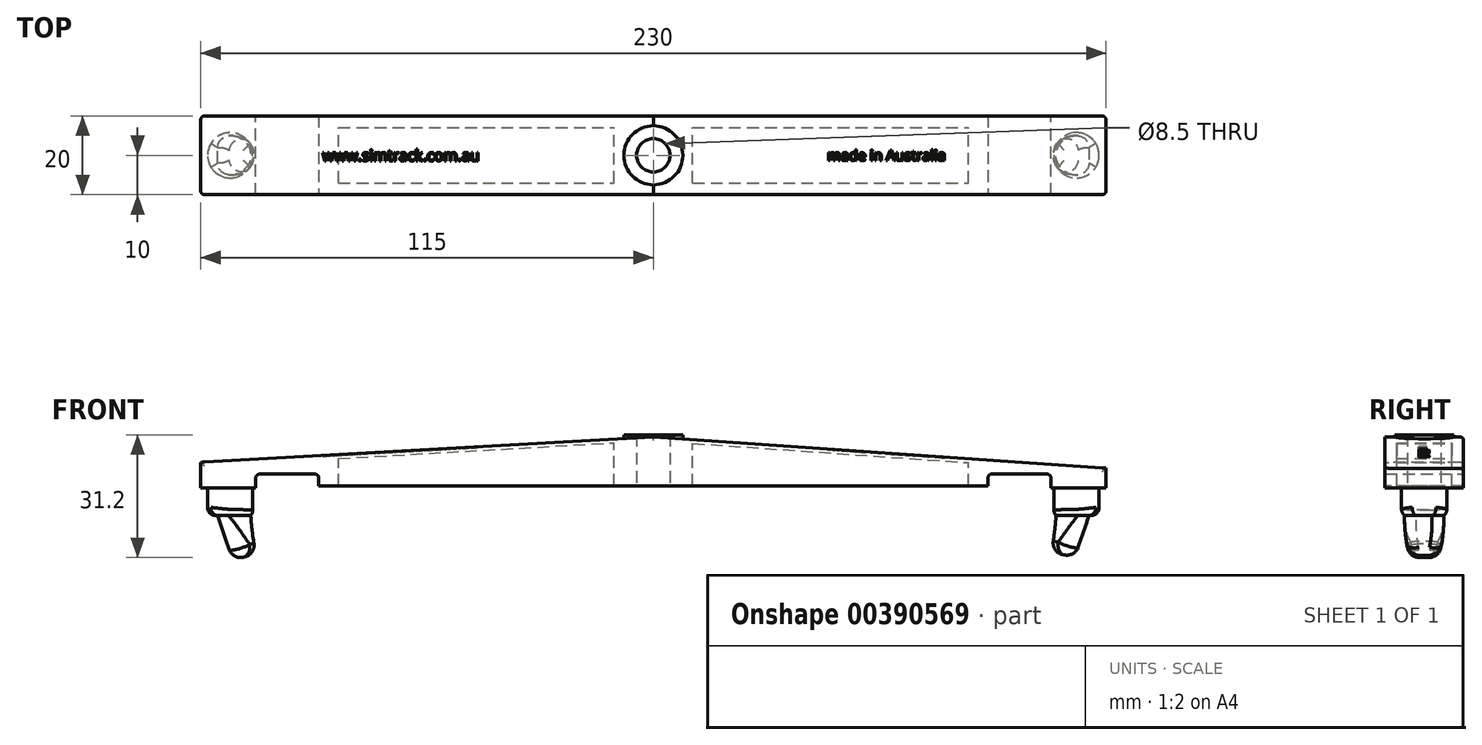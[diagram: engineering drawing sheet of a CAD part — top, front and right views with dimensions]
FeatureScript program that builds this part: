
annotation { "Feature Type Name" : "Feature", "Feature Type Description" : "" }
export const myFeature = defineFeature(function(context is Context, id is Id, definition is map)
    precondition{}
    {
        {
            var Q0;
            Q0=qCreatedBy(makeId("Top.planeOp"),FACE);
            var sketch = newSketch(context, id + "F0", { "sketchPlane" : qUnion([Q0])});
            skCircle(sketch, "E0", {"center": v(0, 0) * mm, "radius": 4.25 * mm});
            skLineSegment(sketch, "E1.bottom", {"start": v(115, -10) * mm, "end": v(-115, -10) * mm});
            skLineSegment(sketch, "E1.top", {"start": v(115, 10) * mm, "end": v(-115, 10) * mm});
            skLineSegment(sketch, "E1.left", {"start": v(115, -10) * mm, "end": v(115, 10) * mm});
            skLineSegment(sketch, "E1.right", {"start": v(-115, -10) * mm, "end": v(-115, 10) * mm});
            skPoint(sketch, "E2.visualSharp", {"position": v(-115, 10) * mm});
            skLineSegment(sketch, "E2.filletArc", {"start": v(-115, 10) * mm, "end": v(-115, 10) * mm});
            skPoint(sketch, "E3.visualSharp", {"position": v(-115, -10) * mm});
            skLineSegment(sketch, "E3.filletArc", {"start": v(-115, -10) * mm, "end": v(-115, -10) * mm});
            skPoint(sketch, "E4.visualSharp", {"position": v(115, 10) * mm});
            skLineSegment(sketch, "E4.filletArc", {"start": v(115, 10) * mm, "end": v(115, 10) * mm});
            skPoint(sketch, "E5.visualSharp", {"position": v(115, -10) * mm});
            skLineSegment(sketch, "E5.filletArc", {"start": v(115, -10) * mm, "end": v(115, -10) * mm});
            skLineSegment(sketch, "E6.bottom", {"start": v(80, 7) * mm, "end": v(10, 7) * mm});
            skLineSegment(sketch, "E6.top", {"start": v(80, -7) * mm, "end": v(10, -7) * mm});
            skLineSegment(sketch, "E6.left", {"start": v(80, 7) * mm, "end": v(80, -7) * mm});
            skLineSegment(sketch, "E6.right", {"start": v(10, 7) * mm, "end": v(10, -7) * mm});
            skLineSegment(sketch, "E7.bottom", {"start": v(-10, 7) * mm, "end": v(-80, 7) * mm});
            skLineSegment(sketch, "E7.top", {"start": v(-10, -7) * mm, "end": v(-80, -7) * mm});
            skLineSegment(sketch, "E7.left", {"start": v(-10, 7) * mm, "end": v(-10, -7) * mm});
            skLineSegment(sketch, "E7.right", {"start": v(-80, 7) * mm, "end": v(-80, -7) * mm});
            skCircle(sketch, "E8", {"center": v(0, 0) * mm, "radius": 7.5 * mm});
            skSolve(sketch);
        }
        {
            var Q0;
            Q0=makeQuery(id+"F0.imprint","IMPRINT",FACE,{"disambiguationData":[TD([[makeQuery(id+"F0.imprint","IMPRINT",EDGE,{"derivedFrom":sQuery(id+"F0.wireOp",EDGE,"E1.bottom")}),-1.0]])]});
            var Q1;
            Q1=makeQuery(id+"F0.imprint","IMPRINT",FACE,{"disambiguationData":[TD([[makeQuery(id+"F0.imprint","IMPRINT",EDGE,{"derivedFrom":sQuery(id+"F0.wireOp",EDGE,"q9BRd2um-oMs7-7MK2-WjCr-aT8UQEt5jsp8")}),-1.0]])]});
            var Q2;
            {var subQ0=sQuery(id+"F0.wireOp",EDGE,"CfEYtvD2-7vdv-HU4w-jJwD-IvnwvT9jjSvh.right");var subQ1=sQuery(id+"F0.wireOp",EDGE,"TnjMtal5-3gMc-DNrO-T4Mg-M14iXYZFMKTD");var subQ2=makeQuery(id+"F0.imprint","INTERSECT",VERTEX,{"disambiguationData":[OD(0.0)],"derivedFrom":[subQ1,subQ0]});Q2=makeQuery(id+"F0.imprint","IMPRINT",FACE,{"disambiguationData":[TD([[makeQuery(id+"F0.imprint","IMPRINT",EDGE,{"disambiguationData":[TD([[subQ2,1.0]])],"derivedFrom":subQ1}),1.0]])]});}
            var Q3;
            {var subQ0=sQuery(id+"F0.wireOp",EDGE,"CfEYtvD2-7vdv-HU4w-jJwD-IvnwvT9jjSvh.left");var subQ1=sQuery(id+"F0.wireOp",EDGE,"O0jPoW7s-RU5z-iA6U-w5ju-wIfl1B3ZVbkh");var subQ2=makeQuery(id+"F0.imprint","INTERSECT",VERTEX,{"disambiguationData":[OD(0.0)],"derivedFrom":[subQ1,subQ0]});Q3=makeQuery(id+"F0.imprint","IMPRINT",FACE,{"disambiguationData":[TD([[makeQuery(id+"F0.imprint","IMPRINT",EDGE,{"disambiguationData":[TD([[subQ2,-1.0]])],"derivedFrom":subQ1}),1.0]])]});}
            var Q4;
            {var subQ0=sQuery(id+"F0.wireOp",EDGE,"CfEYtvD2-7vdv-HU4w-jJwD-IvnwvT9jjSvh.right");var subQ1=sQuery(id+"F0.wireOp",EDGE,"TnjMtal5-3gMc-DNrO-T4Mg-M14iXYZFMKTD");var subQ2=makeQuery(id+"F0.imprint","INTERSECT",VERTEX,{"disambiguationData":[OD(0.0)],"derivedFrom":[subQ1,subQ0]});Q4=makeQuery(id+"F0.imprint","IMPRINT",FACE,{"disambiguationData":[TD([[makeQuery(id+"F0.imprint","IMPRINT",EDGE,{"disambiguationData":[TD([[subQ2,-1.0]])],"derivedFrom":subQ1}),1.0]])]});}
            var Q5;
            {var subQ0=sQuery(id+"F0.wireOp",EDGE,"CfEYtvD2-7vdv-HU4w-jJwD-IvnwvT9jjSvh.left");var subQ1=sQuery(id+"F0.wireOp",EDGE,"O0jPoW7s-RU5z-iA6U-w5ju-wIfl1B3ZVbkh");var subQ2=makeQuery(id+"F0.imprint","INTERSECT",VERTEX,{"disambiguationData":[OD(0.0)],"derivedFrom":[subQ1,subQ0]});Q5=makeQuery(id+"F0.imprint","IMPRINT",FACE,{"disambiguationData":[TD([[makeQuery(id+"F0.imprint","IMPRINT",EDGE,{"disambiguationData":[TD([[subQ2,1.0]])],"derivedFrom":subQ1}),1.0]])]});}
            extrude(context, id + "F1", {"entities" : qUnion([Q0, Q1, Q2, Q3, Q4, Q5]), "oppositeDirection" : true, "depth" : 5 * mm, "hasSecondDirection" : true, "secondDirectionOppositeDirection" : false, "secondDirectionDepth" : 8 * mm});
        }
        {
            var Q0;
            Q0=makeQuery(id+"F1.opExtrude","SWEPT_FACE",FACE,{"disambiguationData":[OSD([sQuery(id+"F0.wireOp",EDGE,"E1.bottom")])]});
            var sketch = newSketch(context, id + "F2", { "sketchPlane" : qUnion([Q0])});
            skLineSegment(sketch, "E9", {"start": v(-115, 1.5) * mm, "end": v(0, 8) * mm});
            skLineSegment(sketch, "E10", {"start": v(0, 8) * mm, "end": v(115, 0) * mm});
            skSolve(sketch);
        }
        {
            var Q0;
            {var subQ0=sQuery(id+"F2.wireOp",EDGE,"E10");Q0=makeQuery(id+"F2.imprint","IMPRINT",FACE,{"disambiguationData":[TD([[makeQuery(id+"F2.imprint","IMPRINT",EDGE,{"derivedFrom":subQ0}),1.0]])]});}
            var Q1;
            {var subQ0=sQuery(id+"F2.wireOp",EDGE,"E9");Q1=makeQuery(id+"F2.imprint","IMPRINT",FACE,{"disambiguationData":[TD([[makeQuery(id+"F2.imprint","IMPRINT",EDGE,{"derivedFrom":subQ0}),1.0]])]});}
            extrude(context, id + "F3", {"entities" : qUnion([Q0, Q1]), "operationType" : NewBodyOperationType.REMOVE, "oppositeDirection" : true, "depth" : 25 * mm});
        }
        {
            var Q0;
            Q0=makeQuery(id+"F0.imprint","IMPRINT",FACE,{"disambiguationData":[TD([[makeQuery(id+"F0.imprint","IMPRINT",EDGE,{"derivedFrom":sQuery(id+"F0.wireOp",EDGE,"E0")}),-1.0]])]});
            var Q1;
            Q1=makeQuery(id+"F0.imprint","IMPRINT",FACE,{"disambiguationData":[TD([[makeQuery(id+"F0.imprint","IMPRINT",EDGE,{"derivedFrom":sQuery(id+"F0.wireOp",EDGE,"E0")}),1.0]])]});
            extrude(context, id + "F4", {"entities" : qUnion([Q0, Q1]), "operationType" : NewBodyOperationType.ADD, "oppositeDirection" : true, "depth" : 5 * mm});
        }
        {
            var Q0;
            Q0=makeQuery(id+"F0.imprint","IMPRINT",FACE,{"disambiguationData":[TD([[makeQuery(id+"F0.imprint","IMPRINT",EDGE,{"derivedFrom":sQuery(id+"F0.wireOp",EDGE,"E0")}),1.0]])]});
            extrude(context, id + "F5", {"entities" : qUnion([Q0]), "operationType" : NewBodyOperationType.REMOVE, "depth" : 8 * mm, "hasSecondDirection" : true, "secondDirectionOppositeDirection" : true, "secondDirectionDepth" : 5 * mm});
        }
        {
            var Q0;
            Q0=makeQuery(id+"F1.opExtrude","SWEPT_FACE",FACE,{"disambiguationData":[OSD([sQuery(id+"F0.wireOp",EDGE,"E1.bottom")])]});
            var sketch = newSketch(context, id + "F6", { "sketchPlane" : qUnion([Q0])});
            skSolve(sketch);
        }
        {
            var Q0;
            Q0=makeQuery(id+"F1.opExtrude","SWEPT_FACE",FACE,{"disambiguationData":[OSD([sQuery(id+"F0.wireOp",EDGE,"E1.top")])]});
            var sketch = newSketch(context, id + "F7", { "sketchPlane" : qUnion([Q0])});
            skLineSegment(sketch, "E11", {"start": v(-115, -5) * mm, "end": v(-101, -5) * mm});
            skLineSegment(sketch, "E12", {"start": v(-101, -5) * mm, "end": v(-101, -1.5) * mm});
            skLineSegment(sketch, "E13", {"start": v(-101, -1.5) * mm, "end": v(-85, -1.5) * mm});
            skLineSegment(sketch, "E14", {"start": v(-85, -1.5) * mm, "end": v(-85, -5) * mm});
            skLineSegment(sketch, "E15", {"start": v(-85, -5) * mm, "end": v(-101, -5) * mm});
            skLineSegment(sketch, "E16", {"start": v(115, -5) * mm, "end": v(101, -5) * mm});
            skLineSegment(sketch, "E17", {"start": v(101, -5) * mm, "end": v(101, -1.5) * mm});
            skLineSegment(sketch, "E18", {"start": v(101, -1.5) * mm, "end": v(85, -1.5) * mm});
            skLineSegment(sketch, "E19", {"start": v(85, -1.5) * mm, "end": v(85, -5) * mm});
            skLineSegment(sketch, "E20", {"start": v(85, -5) * mm, "end": v(101, -5) * mm});
            skSolve(sketch);
        }
        {
            var Q0;
            Q0=makeQuery(id+"F7.imprint","IMPRINT",FACE,{"disambiguationData":[TD([[makeQuery(id+"F7.imprint","IMPRINT",EDGE,{"derivedFrom":sQuery(id+"F7.wireOp",EDGE,"E12")}),-1.0]])]});
            var Q1;
            Q1=makeQuery(id+"F7.imprint","IMPRINT",FACE,{"disambiguationData":[TD([[makeQuery(id+"F7.imprint","IMPRINT",EDGE,{"derivedFrom":sQuery(id+"F7.wireOp",EDGE,"E17")}),1.0]])]});
            extrude(context, id + "F8", {"entities" : qUnion([Q0, Q1]), "operationType" : NewBodyOperationType.REMOVE, "oppositeDirection" : true, "depth" : 25 * mm});
        }
        {
            var Q0;
            Q0=makeQuery(id+"F3.boolean.opBoolean","COPY",FACE,{"derivedFrom":makeQuery(id+"F3.opExtrude","SWEPT_FACE",FACE,{"disambiguationData":[OSD([sQuery(id+"F2.wireOp",EDGE,"E9")])]})});
            var sketch = newSketch(context, id + "F9", { "sketchPlane" : qUnion([Q0])});
            skCircle(sketch, "E21", {"center": v(-107.72, 0) * mm, "radius": 5 * mm});
            skSolve(sketch);
        }
        {
            var Q0;
            Q0=makeQuery(id+"F9.imprint","IMPRINT",FACE,{"disambiguationData":[TD([[makeQuery(id+"F9.imprint","IMPRINT",EDGE,{"derivedFrom":sQuery(id+"F9.wireOp",EDGE,"E21")}),1.0]])]});
            extrude(context, id + "F10", {"entities" : qUnion([Q0]), "operationType" : NewBodyOperationType.ADD, "oppositeDirection" : true, "depth" : 8 * mm});
        }
        {
            var Q0;
            Q0=makeQuery(id+"F3.boolean.opBoolean","COPY",FACE,{"derivedFrom":makeQuery(id+"F3.opExtrude","SWEPT_FACE",FACE,{"disambiguationData":[OSD([sQuery(id+"F2.wireOp",EDGE,"E10")])]})});
            var sketch = newSketch(context, id + "F11", { "sketchPlane" : qUnion([Q0])});
            skCircle(sketch, "E22", {"center": v(107.7, 0) * mm, "radius": 5 * mm});
            skSolve(sketch);
        }
        {
            var Q0;
            Q0=makeQuery(id+"F11.imprint","IMPRINT",FACE,{"disambiguationData":[TD([[makeQuery(id+"F11.imprint","IMPRINT",EDGE,{"derivedFrom":sQuery(id+"F11.wireOp",EDGE,"E22")}),1.0]])]});
            extrude(context, id + "F12", {"entities" : qUnion([Q0]), "operationType" : NewBodyOperationType.ADD, "oppositeDirection" : true, "depth" : 6 * mm});
        }
        {
            var Q0;
            Q0=makeQuery(id+"F0.imprint","IMPRINT",FACE,{"disambiguationData":[TD([[makeQuery(id+"F0.imprint","IMPRINT",EDGE,{"derivedFrom":sQuery(id+"F0.wireOp",EDGE,"E7.bottom")}),1.0]])]});
            var Q1;
            Q1=makeQuery(id+"F0.imprint","IMPRINT",FACE,{"disambiguationData":[TD([[makeQuery(id+"F0.imprint","IMPRINT",EDGE,{"derivedFrom":sQuery(id+"F0.wireOp",EDGE,"E6.bottom")}),1.0]])]});
            extrude(context, id + "F13", {"entities" : qUnion([Q0, Q1]), "operationType" : NewBodyOperationType.REMOVE, "depth" : 29 * mm, "hasDraft" : true, "draftAngle" : 3 * degree});
        }
        {
            var Q0;
            {var subQ0=sQuery(id+"F0.wireOp",EDGE,"E1.bottom");Q0=makeQuery(id+"F6.imprint","IMPRINT",FACE,{"disambiguationData":[TD([[makeQuery(id+"F6.imprint","IMPRINT",EDGE,{"derivedFrom":makeQuery(id+"F1.opExtrude","CAP_EDGE",EDGE,{"disambiguationData":[OSD([subQ0])],"isStart":false})}),-1.0]])]});}
            var sketch = newSketch(context, id + "F14", { "sketchPlane" : qUnion([Q0])});
            skSolve(sketch);
        }
        {
            var Q0;
            Q0=makeQuery(id+"F1.opExtrude","SWEPT_FACE",FACE,{"disambiguationData":[OSD([sQuery(id+"F0.wireOp",EDGE,"E1.top")])]});
            extrude(context, id + "F15", {"entities" : qUnion([Q0]), "operationType" : NewBodyOperationType.ADD, "oppositeDirection" : true, "depth" : 20 * mm});
        }
        {
            var Q0;
            Q0=makeQuery(id+"F0.imprint","IMPRINT",FACE,{"disambiguationData":[TD([[makeQuery(id+"F0.imprint","IMPRINT",EDGE,{"derivedFrom":sQuery(id+"F0.wireOp",EDGE,"E7.bottom")}),1.0]])]});
            var Q1;
            Q1=makeQuery(id+"F0.imprint","IMPRINT",FACE,{"disambiguationData":[TD([[makeQuery(id+"F0.imprint","IMPRINT",EDGE,{"derivedFrom":sQuery(id+"F0.wireOp",EDGE,"E6.bottom")}),1.0]])]});
            extrude(context, id + "F16", {"entities" : qUnion([Q0, Q1]), "operationType" : NewBodyOperationType.REMOVE, "oppositeDirection" : true, "depth" : 25 * mm, "hasSecondDirection" : true, "secondDirectionOppositeDirection" : false, "secondDirectionDepth" : 25 * mm});
        }
        {
            var Q0;
            Q0=makeQuery(id+"F0.imprint","IMPRINT",FACE,{"disambiguationData":[TD([[makeQuery(id+"F0.imprint","IMPRINT",EDGE,{"derivedFrom":sQuery(id+"F0.wireOp",EDGE,"E0")}),-1.0]])]});
            extrude(context, id + "F17", {"entities" : qUnion([Q0]), "operationType" : NewBodyOperationType.ADD, "depth" : 8.5 * mm});
        }
        {
            var Q0;
            Q0=makeQuery(id+"F0.imprint","IMPRINT",FACE,{"disambiguationData":[TD([[makeQuery(id+"F0.imprint","IMPRINT",EDGE,{"derivedFrom":sQuery(id+"F0.wireOp",EDGE,"E0")}),1.0]])]});
            extrude(context, id + "F18", {"entities" : qUnion([Q0]), "operationType" : NewBodyOperationType.REMOVE, "oppositeDirection" : true, "depth" : 25 * mm, "hasSecondDirection" : true, "secondDirectionOppositeDirection" : false, "secondDirectionDepth" : 25 * mm});
        }
        {
            var Q0;
            Q0=makeQuery(id+"F3.boolean.opBoolean","COPY",EDGE,{"derivedFrom":makeQuery(id+"F3.opExtrude","SWEPT_EDGE",EDGE,{"disambiguationData":[OSD([sQuery(id+"F0.wireOp",EDGE,"E1.bottom"),sQuery(id+"F0.wireOp",EDGE,"E1.left"),sQuery(id+"F2.wireOp",EDGE,"E10")])]})});
            var Q1;
            Q1=makeQuery(id+"F3.boolean.opBoolean","INTERSECT",EDGE,{"derivedFrom":[makeQuery(id+"F1.opExtrude","SWEPT_FACE",FACE,{"disambiguationData":[OSD([sQuery(id+"F0.wireOp",EDGE,"E1.top")])]}),makeQuery(id+"F3.opExtrude","SWEPT_FACE",FACE,{"disambiguationData":[OSD([sQuery(id+"F2.wireOp",EDGE,"E10")])]})]});
            var Q2;
            Q2=makeQuery(id+"F3.boolean.opBoolean","INTERSECT",EDGE,{"derivedFrom":[makeQuery(id+"F1.opExtrude","SWEPT_FACE",FACE,{"disambiguationData":[OSD([sQuery(id+"F0.wireOp",EDGE,"E1.top")])]}),makeQuery(id+"F3.opExtrude","SWEPT_FACE",FACE,{"disambiguationData":[OSD([sQuery(id+"F2.wireOp",EDGE,"E9")])]})]});
            var Q3;
            Q3=makeQuery(id+"F3.boolean.opBoolean","COPY",EDGE,{"derivedFrom":makeQuery(id+"F3.opExtrude","SWEPT_EDGE",EDGE,{"disambiguationData":[OSD([sQuery(id+"F0.wireOp",EDGE,"E1.bottom"),sQuery(id+"F0.wireOp",EDGE,"E1.right"),sQuery(id+"F2.wireOp",EDGE,"E9")])]})});
            var Q4;
            Q4=makeQuery(id+"F1.opExtrude","SWEPT_EDGE",EDGE,{"disambiguationData":[OSD([sQuery(id+"F0.wireOp",EDGE,"E1.bottom"),sQuery(id+"F0.wireOp",EDGE,"E1.right")])]});
            var Q5;
            Q5=makeQuery(id+"F1.opExtrude","SWEPT_EDGE",EDGE,{"disambiguationData":[OSD([sQuery(id+"F0.wireOp",EDGE,"E1.top"),sQuery(id+"F0.wireOp",EDGE,"E1.right")])]});
            var Q6;
            Q6=makeQuery(id+"F3.boolean.opBoolean","COPY",EDGE,{"derivedFrom":makeQuery(id+"F3.opExtrude","CAP_EDGE",EDGE,{"disambiguationData":[OSD([sQuery(id+"F2.wireOp",EDGE,"E10")])],"isStart":true})});
            var Q7;
            Q7=makeQuery(id+"F3.boolean.opBoolean","COPY",EDGE,{"derivedFrom":makeQuery(id+"F3.opExtrude","CAP_EDGE",EDGE,{"disambiguationData":[OSD([sQuery(id+"F2.wireOp",EDGE,"E9")])],"isStart":true})});
            var Q8;
            Q8=makeQuery(id+"F1.opExtrude","SWEPT_EDGE",EDGE,{"disambiguationData":[OSD([sQuery(id+"F0.wireOp",EDGE,"E1.top"),sQuery(id+"F0.wireOp",EDGE,"E1.left")])]});
            var Q9;
            Q9=makeQuery(id+"F1.opExtrude","SWEPT_EDGE",EDGE,{"disambiguationData":[OSD([sQuery(id+"F0.wireOp",EDGE,"E1.bottom"),sQuery(id+"F0.wireOp",EDGE,"E1.left")])]});
            fillet(context, id + "F19", {"entities" : qUnion([Q0, Q1, Q2, Q3, Q4, Q5, Q6, Q7, Q8, Q9]), "radius" : 1 * mm, "tangentPropagation" : true, "allowEdgeOverflow" : false});
        }
        {
            var Q0;
            Q0=makeQuery(id+"F8.boolean.opBoolean","COPY",EDGE,{"derivedFrom":makeQuery(id+"F8.opExtrude","SWEPT_EDGE",EDGE,{"disambiguationData":[OSD([sQuery(id+"F7.wireOp",EDGE,"E18"),sQuery(id+"F7.wireOp",EDGE,"E19")])]})});
            var Q1;
            Q1=makeQuery(id+"F8.boolean.opBoolean","COPY",EDGE,{"derivedFrom":makeQuery(id+"F8.opExtrude","SWEPT_EDGE",EDGE,{"disambiguationData":[OSD([sQuery(id+"F7.wireOp",EDGE,"E17"),sQuery(id+"F7.wireOp",EDGE,"E18")])]})});
            var Q2;
            Q2=makeQuery(id+"F8.boolean.opBoolean","COPY",EDGE,{"derivedFrom":makeQuery(id+"F8.opExtrude","SWEPT_EDGE",EDGE,{"disambiguationData":[OSD([sQuery(id+"F7.wireOp",EDGE,"E13"),sQuery(id+"F7.wireOp",EDGE,"E14")])]})});
            var Q3;
            Q3=makeQuery(id+"F8.boolean.opBoolean","COPY",EDGE,{"derivedFrom":makeQuery(id+"F8.opExtrude","SWEPT_EDGE",EDGE,{"disambiguationData":[OSD([sQuery(id+"F7.wireOp",EDGE,"E12"),sQuery(id+"F7.wireOp",EDGE,"E13")])]})});
            fillet(context, id + "F20", {"entities" : qUnion([Q0, Q1, Q2, Q3]), "radius" : 1 * mm, "tangentPropagation" : true, "allowEdgeOverflow" : false});
        }
        {
            var Q0;
            {var subQ1=sQuery(id+"F0.wireOp",EDGE,"E1.top");var subQ2=sQuery(id+"F2.wireOp",EDGE,"E10");Q0=makeQuery(id+"F17.boolean.opBoolean","SPLIT",FACE,{"disambiguationData":[TD([makeQuery(id+"F1.opExtrude","SWEPT_FACE",FACE,{"disambiguationData":[OSD([sQuery(id+"F0.wireOp",EDGE,"E1.bottom")])]})])],"derivedFrom":makeQuery(id+"F15.boolean.opBoolean","MERGE",FACE,{"derivedFrom":[makeQuery(id+"F3.boolean.opBoolean","COPY",FACE,{"derivedFrom":makeQuery(id+"F3.opExtrude","SWEPT_FACE",FACE,{"disambiguationData":[OSD([subQ2])]})}),makeQuery(id+"F15.opExtrude","SWEPT_FACE",FACE,{"disambiguationData":[OSD([subQ1,subQ2])]})]})});}
            var sketch = newSketch(context, id + "F21", { "sketchPlane" : qUnion([Q0])});
            skSolve(sketch);
        }
        {
            var Q0;
            Q0=makeQuery(id+"F12.opExtrude","CAP_FACE",FACE,{"disambiguationData":[OSD([sQuery(id+"F0.wireOp",EDGE,"O0jPoW7s-RU5z-iA6U-w5ju-wIfl1B3ZVbkh"),sQuery(id+"F2.wireOp",EDGE,"E10"),sQuery(id+"F11.wireOp",EDGE,"E22")])],"isStart":false});
            var Q1;
            {var subQ0=sQuery(id+"F0.wireOp",EDGE,"E6.right");var subQ1=makeQuery(id+"F8.opExtrude","SWEPT_FACE",FACE,{"disambiguationData":[OSD([sQuery(id+"F7.wireOp",EDGE,"E14")])]});var subQ2=sQuery(id+"F0.wireOp",EDGE,"E1.top");var subQ4=sQuery(id+"F0.wireOp",EDGE,"E8");var subQ5=makeQuery(id+"F4.opExtrude","CAP_FACE",FACE,{"disambiguationData":[OSD([subQ4])],"isStart":false});var subQ6=sQuery(id+"F0.wireOp",EDGE,"E7.right");var subQ7=sQuery(id+"F0.wireOp",EDGE,"E7.left");var subQ8=sQuery(id+"F0.wireOp",EDGE,"E7.top");var subQ9=sQuery(id+"F0.wireOp",EDGE,"E7.bottom");var subQ10=sQuery(id+"F0.wireOp",EDGE,"E6.left");var subQ11=sQuery(id+"F0.wireOp",EDGE,"E6.top");var subQ12=sQuery(id+"F0.wireOp",EDGE,"E6.bottom");var subQ13=sQuery(id+"F0.wireOp",EDGE,"E1.bottom");var subQ14=makeQuery(id+"F1.opExtrude","CAP_FACE",FACE,{"disambiguationData":[OSD([sQuery(id+"F0.wireOp",EDGE,"O0jPoW7s-RU5z-iA6U-w5ju-wIfl1B3ZVbkh"),sQuery(id+"F0.wireOp",EDGE,"TnjMtal5-3gMc-DNrO-T4Mg-M14iXYZFMKTD"),subQ13,subQ2,sQuery(id+"F0.wireOp",EDGE,"E1.left"),sQuery(id+"F0.wireOp",EDGE,"E1.right"),subQ12,subQ11,subQ10,subQ0,subQ9,subQ8,subQ7,subQ6,subQ4])],"isStart":false});Q1=makeQuery(id+"F16.boolean.opBoolean","INTERSECT",EDGE,{"derivedFrom":[makeQuery(id+"F15.boolean.opBoolean","MERGE",FACE,{"derivedFrom":[makeQuery(id+"F8.boolean.opBoolean","SPLIT",FACE,{"disambiguationData":[TD([makeQuery(id+"F1.opExtrude","SWEPT_FACE",FACE,{"disambiguationData":[OSD([subQ12])]})])],"derivedFrom":makeQuery(id+"F4.boolean.opBoolean","MERGE",FACE,{"derivedFrom":[subQ14,subQ5]})}),makeQuery(id+"F15.opExtrude","SWEPT_FACE",FACE,{"disambiguationData":[OSD([subQ2]),TDD([makeQuery(id+"F8.boolean.opBoolean","SPLIT",EDGE,{"disambiguationData":[TD([subQ1])],"derivedFrom":makeQuery(id+"F1.opExtrude","CAP_EDGE",EDGE,{"disambiguationData":[OSD([subQ2])],"isStart":false})})])]})]}),makeQuery(id+"F16.opExtrude","SWEPT_FACE",FACE,{"disambiguationData":[OSD([subQ0])]})]});}
            revolve(context, id + "F22", {"operationType" : NewBodyOperationType.ADD, "entities" : qUnion([Q0]), "axis" : qUnion([Q1]), "revolveType" : RevolveType.ONE_DIRECTION, "oppositeDirection" : true, "angle" : 10 * degree});
        }
        {
            var Q0;
            Q0=makeQuery(id+"F10.opExtrude","CAP_FACE",FACE,{"disambiguationData":[OSD([sQuery(id+"F0.wireOp",EDGE,"TnjMtal5-3gMc-DNrO-T4Mg-M14iXYZFMKTD"),sQuery(id+"F2.wireOp",EDGE,"E9"),sQuery(id+"F9.wireOp",EDGE,"E21")])],"isStart":false});
            var Q1;
            {var subQ0=sQuery(id+"F0.wireOp",EDGE,"E7.left");var subQ1=makeQuery(id+"F8.opExtrude","SWEPT_FACE",FACE,{"disambiguationData":[OSD([sQuery(id+"F7.wireOp",EDGE,"E14")])]});var subQ2=sQuery(id+"F0.wireOp",EDGE,"E1.top");var subQ4=sQuery(id+"F0.wireOp",EDGE,"E8");var subQ5=makeQuery(id+"F4.opExtrude","CAP_FACE",FACE,{"disambiguationData":[OSD([subQ4])],"isStart":false});var subQ6=sQuery(id+"F0.wireOp",EDGE,"E7.right");var subQ7=sQuery(id+"F0.wireOp",EDGE,"E7.top");var subQ8=sQuery(id+"F0.wireOp",EDGE,"E7.bottom");var subQ9=sQuery(id+"F0.wireOp",EDGE,"E6.right");var subQ10=sQuery(id+"F0.wireOp",EDGE,"E6.left");var subQ11=sQuery(id+"F0.wireOp",EDGE,"E6.top");var subQ12=sQuery(id+"F0.wireOp",EDGE,"E6.bottom");var subQ13=sQuery(id+"F0.wireOp",EDGE,"E1.bottom");var subQ14=makeQuery(id+"F1.opExtrude","CAP_FACE",FACE,{"disambiguationData":[OSD([sQuery(id+"F0.wireOp",EDGE,"O0jPoW7s-RU5z-iA6U-w5ju-wIfl1B3ZVbkh"),sQuery(id+"F0.wireOp",EDGE,"TnjMtal5-3gMc-DNrO-T4Mg-M14iXYZFMKTD"),subQ13,subQ2,sQuery(id+"F0.wireOp",EDGE,"E1.left"),sQuery(id+"F0.wireOp",EDGE,"E1.right"),subQ12,subQ11,subQ10,subQ9,subQ8,subQ7,subQ0,subQ6,subQ4])],"isStart":false});Q1=makeQuery(id+"F16.boolean.opBoolean","INTERSECT",EDGE,{"derivedFrom":[makeQuery(id+"F15.boolean.opBoolean","MERGE",FACE,{"derivedFrom":[makeQuery(id+"F8.boolean.opBoolean","SPLIT",FACE,{"disambiguationData":[TD([makeQuery(id+"F1.opExtrude","SWEPT_FACE",FACE,{"disambiguationData":[OSD([subQ12])]})])],"derivedFrom":makeQuery(id+"F4.boolean.opBoolean","MERGE",FACE,{"derivedFrom":[subQ14,subQ5]})}),makeQuery(id+"F15.opExtrude","SWEPT_FACE",FACE,{"disambiguationData":[OSD([subQ2]),TDD([makeQuery(id+"F8.boolean.opBoolean","SPLIT",EDGE,{"disambiguationData":[TD([subQ1])],"derivedFrom":makeQuery(id+"F1.opExtrude","CAP_EDGE",EDGE,{"disambiguationData":[OSD([subQ2])],"isStart":false})})])]})]}),makeQuery(id+"F16.opExtrude","SWEPT_FACE",FACE,{"disambiguationData":[OSD([subQ0])]})]});}
            revolve(context, id + "F23", {"operationType" : NewBodyOperationType.ADD, "entities" : qUnion([Q0]), "axis" : qUnion([Q1]), "revolveType" : RevolveType.ONE_DIRECTION, "angle" : 10 * degree});
        }
        {
            var Q0;
            {var subQ0=sQuery(id+"F0.wireOp",EDGE,"E1.bottom");Q0=makeQuery(id+"F14.imprint","IMPRINT",FACE,{"disambiguationData":[TD([[makeQuery(id+"F14.imprint","IMPRINT",EDGE,{"derivedFrom":makeQuery(id+"F6.imprint","IMPRINT",EDGE,{"derivedFrom":makeQuery(id+"F1.opExtrude","CAP_EDGE",EDGE,{"disambiguationData":[OSD([subQ0])],"isStart":false})})}),-1.0]])]});}
            var sketch = newSketch(context, id + "F24", { "sketchPlane" : qUnion([Q0])});
            skLineSegment(sketch, "E23", {"start": v(-113, -5.27) * mm, "end": v(-105, -28.6) * mm});
            skLineSegment(sketch, "E24", {"start": v(-105, -28.6) * mm, "end": v(-114.46, -31.85) * mm});
            skLineSegment(sketch, "E25", {"start": v(-114.46, -31.85) * mm, "end": v(-123.26, -6.19) * mm});
            skLineSegment(sketch, "E26", {"start": v(-123.26, -6.19) * mm, "end": v(-113, -5.27) * mm});
            skLineSegment(sketch, "E27", {"start": v(-105, -28.6) * mm, "end": v(105, -28.6) * mm});
            skLineSegment(sketch, "E28", {"start": v(105, -28.6) * mm, "end": v(113, -5.27) * mm});
            skLineSegment(sketch, "E29", {"start": v(113, -5.27) * mm, "end": v(122.46, -8.5) * mm});
            skLineSegment(sketch, "E30", {"start": v(122.46, -8.5) * mm, "end": v(112.46, -37.7) * mm});
            skLineSegment(sketch, "E31", {"start": v(112.46, -37.7) * mm, "end": v(105, -28.6) * mm});
            skLineSegment(sketch, "E32", {"start": v(-136.8, -16.49) * mm, "end": v(163.26, -16.49) * mm});
            skPoint(sketch, "E33.orphan", {"position": v(-142.98, -6.19) * mm});
            skSolve(sketch);
        }
        {
            var Q0;
            Q0=makeQuery(id+"F24.imprint","IMPRINT",FACE,{"disambiguationData":[TD([[makeQuery(id+"F24.imprint","IMPRINT",EDGE,{"derivedFrom":sQuery(id+"F24.wireOp",EDGE,"E23")}),-1.0]])]});
            var Q1;
            Q1=makeQuery(id+"F24.imprint","IMPRINT",FACE,{"disambiguationData":[TD([[makeQuery(id+"F24.imprint","IMPRINT",EDGE,{"derivedFrom":sQuery(id+"F24.wireOp",EDGE,"E28")}),-1.0]])]});
            extrude(context, id + "F25", {"entities" : qUnion([Q0, Q1]), "operationType" : NewBodyOperationType.REMOVE, "oppositeDirection" : true, "depth" : 25 * mm});
        }
        {
            var Q0;
            {var subQ0=sQuery(id+"F0.wireOp",EDGE,"E1.bottom");Q0=makeQuery(id+"F14.imprint","IMPRINT",FACE,{"disambiguationData":[TD([[makeQuery(id+"F14.imprint","IMPRINT",EDGE,{"derivedFrom":makeQuery(id+"F6.imprint","IMPRINT",EDGE,{"derivedFrom":makeQuery(id+"F1.opExtrude","CAP_EDGE",EDGE,{"disambiguationData":[OSD([subQ0])],"isStart":false})})}),-1.0]])]});}
            var sketch = newSketch(context, id + "F26", { "sketchPlane" : qUnion([Q0])});
            skLineSegment(sketch, "E34.bottom", {"start": v(85.5, -8.11) * mm, "end": v(-85.5, -8.11) * mm});
            skLineSegment(sketch, "E34.top", {"start": v(85.5, -4.5) * mm, "end": v(-85.5, -4.5) * mm});
            skLineSegment(sketch, "E34.left", {"start": v(85.5, -8.11) * mm, "end": v(85.5, -4.5) * mm});
            skLineSegment(sketch, "E34.right", {"start": v(-85.5, -8.11) * mm, "end": v(-85.5, -4.5) * mm});
            skPoint(sketch, "E34.middle", {"position": v(0, -6.3) * mm});
            skSolve(sketch);
        }
        {
            var Q0;
            {var subQ0=sQuery(id+"F26.wireOp",EDGE,"E34.top");Q0=makeQuery(id+"F26.imprint","IMPRINT",FACE,{"disambiguationData":[TD([[makeQuery(id+"F26.imprint","IMPRINT",EDGE,{"derivedFrom":subQ0}),1.0]])]});}
            extrude(context, id + "F27", {"entities" : qUnion([Q0]), "operationType" : NewBodyOperationType.REMOVE, "oppositeDirection" : true, "depth" : 25 * mm});
        }
        {
            var Q0;
            Q0=makeQuery(id+"F25.boolean.opBoolean","INTERSECT",EDGE,{"derivedFrom":[makeQuery(id+"F23.opRevolve","SWEPT_FACE",FACE,{"disambiguationData":[OSD([sQuery(id+"F9.wireOp",EDGE,"E21")])]}),makeQuery(id+"F25.opExtrude","SWEPT_FACE",FACE,{"disambiguationData":[OSD([sQuery(id+"F24.wireOp",EDGE,"E23")])]})]});
            var Q1;
            Q1=makeQuery(id+"F23.opRevolve","CAP_EDGE",EDGE,{"disambiguationData":[OSD([sQuery(id+"F9.wireOp",EDGE,"E21")]),OD(1.0)],"isStart":false});
            var Q2;
            Q2=makeQuery(id+"F25.boolean.opBoolean","INTERSECT",EDGE,{"disambiguationData":[OD(1.0)],"derivedFrom":[makeQuery(id+"F23.opRevolve","CAP_FACE",FACE,{"disambiguationData":[OSD([sQuery(id+"F0.wireOp",EDGE,"TnjMtal5-3gMc-DNrO-T4Mg-M14iXYZFMKTD"),sQuery(id+"F2.wireOp",EDGE,"E9"),sQuery(id+"F9.wireOp",EDGE,"E21")])],"isStart":false}),makeQuery(id+"F25.opExtrude","SWEPT_FACE",FACE,{"disambiguationData":[OSD([sQuery(id+"F24.wireOp",EDGE,"E23")])]})]});
            var Q3;
            Q3=makeQuery(id+"F25.boolean.opBoolean","INTERSECT",EDGE,{"disambiguationData":[OD(0.0)],"derivedFrom":[makeQuery(id+"F23.opRevolve","CAP_FACE",FACE,{"disambiguationData":[OSD([sQuery(id+"F0.wireOp",EDGE,"TnjMtal5-3gMc-DNrO-T4Mg-M14iXYZFMKTD"),sQuery(id+"F2.wireOp",EDGE,"E9"),sQuery(id+"F9.wireOp",EDGE,"E21")])],"isStart":false}),makeQuery(id+"F25.opExtrude","SWEPT_FACE",FACE,{"disambiguationData":[OSD([sQuery(id+"F24.wireOp",EDGE,"E23")])]})]});
            var Q4;
            Q4=makeQuery(id+"F22.opRevolve","CAP_EDGE",EDGE,{"disambiguationData":[OSD([sQuery(id+"F11.wireOp",EDGE,"E22")]),OD(1.0)],"isStart":false});
            var Q5;
            Q5=makeQuery(id+"F25.boolean.opBoolean","INTERSECT",EDGE,{"derivedFrom":[makeQuery(id+"F22.opRevolve","SWEPT_FACE",FACE,{"disambiguationData":[OSD([sQuery(id+"F11.wireOp",EDGE,"E22")])]}),makeQuery(id+"F25.opExtrude","SWEPT_FACE",FACE,{"disambiguationData":[OSD([sQuery(id+"F24.wireOp",EDGE,"E28")])]})]});
            var Q6;
            Q6=makeQuery(id+"F25.boolean.opBoolean","INTERSECT",EDGE,{"disambiguationData":[OD(1.0)],"derivedFrom":[makeQuery(id+"F22.opRevolve","CAP_FACE",FACE,{"disambiguationData":[OSD([sQuery(id+"F0.wireOp",EDGE,"O0jPoW7s-RU5z-iA6U-w5ju-wIfl1B3ZVbkh"),sQuery(id+"F2.wireOp",EDGE,"E10"),sQuery(id+"F11.wireOp",EDGE,"E22")])],"isStart":false}),makeQuery(id+"F25.opExtrude","SWEPT_FACE",FACE,{"disambiguationData":[OSD([sQuery(id+"F24.wireOp",EDGE,"E28")])]})]});
            var Q7;
            Q7=makeQuery(id+"F25.boolean.opBoolean","INTERSECT",EDGE,{"disambiguationData":[OD(0.0)],"derivedFrom":[makeQuery(id+"F22.opRevolve","CAP_FACE",FACE,{"disambiguationData":[OSD([sQuery(id+"F0.wireOp",EDGE,"O0jPoW7s-RU5z-iA6U-w5ju-wIfl1B3ZVbkh"),sQuery(id+"F2.wireOp",EDGE,"E10"),sQuery(id+"F11.wireOp",EDGE,"E22")])],"isStart":false}),makeQuery(id+"F25.opExtrude","SWEPT_FACE",FACE,{"disambiguationData":[OSD([sQuery(id+"F24.wireOp",EDGE,"E28")])]})]});
            fillet(context, id + "F28", {"entities" : qUnion([Q0, Q1, Q2, Q3, Q4, Q5, Q6, Q7]), "radius" : 3 * mm, "allowEdgeOverflow" : false});
        }
        {
            var Q0;
            Q0=qCreatedBy(makeId("Top.planeOp"),FACE);
            var sketch = newSketch(context, id + "F29", { "sketchPlane" : qUnion([Q0])});
            skLineSegment(sketch, "E35", {"start": v(-136.77, 0) * mm, "end": v(141.95, 0) * mm});
            skCircle(sketch, "E36", {"center": v(107.5, 0) * mm, "radius": 5.75 * mm});
            skCircle(sketch, "E37", {"center": v(-107.5, 0) * mm, "radius": 5.75 * mm});
            skCircle(sketch, "E38", {"center": v(-107.5, 0) * mm, "radius": 2.5 * mm});
            skCircle(sketch, "E39", {"center": v(107.5, 0) * mm, "radius": 2.5 * mm});
            skSolve(sketch);
        }
        {
            var Q0;
            Q0=qSketchRegion(id+"F29",true);
            extrude(context, id + "F30", {"entities" : qUnion([Q0]), "operationType" : NewBodyOperationType.ADD, "oppositeDirection" : true, "depth" : 12 * mm});
        }
        {
            var Q0;
            Q0=makeQuery(id+"F30.opExtrude","CAP_EDGE",EDGE,{"disambiguationData":[OSD([sQuery(id+"F29.wireOp",EDGE,"E37")])],"isStart":false});
            var Q1;
            Q1=makeQuery(id+"F30.opExtrude","CAP_EDGE",EDGE,{"disambiguationData":[OSD([sQuery(id+"F29.wireOp",EDGE,"E36")])],"isStart":false});
            fillet(context, id + "F31", {"entities" : qUnion([Q0, Q1]), "radius" : 2 * mm, "tangentPropagation" : true, "allowEdgeOverflow" : false});
        }
        {
            var Q0;
            {var subQ0=sQuery(id+"F0.wireOp",EDGE,"E1.top");var subQ2=sQuery(id+"F2.wireOp",EDGE,"E9");Q0=makeQuery(id+"F17.boolean.opBoolean","SPLIT",FACE,{"disambiguationData":[TD([makeQuery(id+"F1.opExtrude","SWEPT_FACE",FACE,{"disambiguationData":[OSD([sQuery(id+"F0.wireOp",EDGE,"E1.bottom")])]})])],"derivedFrom":makeQuery(id+"F15.boolean.opBoolean","MERGE",FACE,{"derivedFrom":[makeQuery(id+"F3.boolean.opBoolean","COPY",FACE,{"derivedFrom":makeQuery(id+"F3.opExtrude","SWEPT_FACE",FACE,{"disambiguationData":[OSD([subQ2])]})}),makeQuery(id+"F15.opExtrude","SWEPT_FACE",FACE,{"disambiguationData":[OSD([subQ0,subQ2])]})]})});}
            var sketch = newSketch(context, id + "F32", { "sketchPlane" : qUnion([Q0])});
            skLineSegment(sketch, "E40.bottom", {"start": v(-80.42, 7.86) * mm, "end": v(-8.35, 7.86) * mm});
            skLineSegment(sketch, "E40.top", {"start": v(-80.42, -8.1) * mm, "end": v(-8.35, -8.1) * mm});
            skLineSegment(sketch, "E40.left", {"start": v(-80.42, 7.86) * mm, "end": v(-80.42, -8.1) * mm});
            skLineSegment(sketch, "E40.right", {"start": v(-8.35, 7.86) * mm, "end": v(-8.35, -8.1) * mm});
            skSolve(sketch);
        }
        {
            var Q0;
            Q0=makeQuery(id+"F32.imprint","IMPRINT",FACE,{"disambiguationData":[TD([[makeQuery(id+"F32.imprint","IMPRINT",EDGE,{"derivedFrom":sQuery(id+"F32.wireOp",EDGE,"E40.bottom")}),-1.0]])]});
            var Q1;
            {var subQ0=sQuery(id+"F2.wireOp",EDGE,"E9");var subQ1=makeQuery(id+"F15.boolean.opBoolean","MERGE",FACE,{"derivedFrom":[makeQuery(id+"F3.boolean.opBoolean","COPY",FACE,{"derivedFrom":makeQuery(id+"F3.opExtrude","SWEPT_FACE",FACE,{"disambiguationData":[OSD([subQ0])]})}),makeQuery(id+"F15.opExtrude","SWEPT_FACE",FACE,{"disambiguationData":[OSD([sQuery(id+"F0.wireOp",EDGE,"E1.top"),subQ0])]})]});Q1=makeQuery(id+"F32.imprint","IMPRINT",FACE,{"disambiguationData":[TD([[makeQuery(id+"F32.imprint","IMPRINT",EDGE,{"derivedFrom":makeQuery(id+"F16.boolean.opBoolean","INTERSECT",EDGE,{"derivedFrom":[subQ1,makeQuery(id+"F16.opExtrude","SWEPT_FACE",FACE,{"disambiguationData":[OSD([sQuery(id+"F0.wireOp",EDGE,"E7.bottom")])]})]})}),-1.0]])]});}
            extrude(context, id + "F33", {"entities" : qUnion([Q0, Q1]), "operationType" : NewBodyOperationType.ADD, "oppositeDirection" : true, "depth" : 1 * mm});
        }
        {
            var Q0;
            {var subQ1=sQuery(id+"F2.wireOp",EDGE,"E10");var subQ2=sQuery(id+"F0.wireOp",EDGE,"E1.top");var subQ3=makeQuery(id+"F15.opExtrude","SWEPT_FACE",FACE,{"disambiguationData":[OSD([subQ2,subQ1])]});var subQ4=makeQuery(id+"F3.opExtrude","SWEPT_FACE",FACE,{"disambiguationData":[OSD([subQ1])]});var subQ5=makeQuery(id+"F3.boolean.opBoolean","COPY",FACE,{"derivedFrom":subQ4});var subQ6=makeQuery(id+"F15.boolean.opBoolean","MERGE",FACE,{"derivedFrom":[subQ5,subQ3]});var subQ9=makeQuery(id+"F16.opExtrude","SWEPT_FACE",FACE,{"disambiguationData":[OSD([sQuery(id+"F0.wireOp",EDGE,"E6.bottom")])]});Q0=makeQuery(id+"F21.imprint","IMPRINT",FACE,{"disambiguationData":[TD([[makeQuery(id+"F21.imprint","IMPRINT",EDGE,{"derivedFrom":makeQuery(id+"F16.boolean.opBoolean","INTERSECT",EDGE,{"derivedFrom":[subQ6,subQ9]})}),1.0]])]});}
            var sketch = newSketch(context, id + "F34", { "sketchPlane" : qUnion([Q0])});
            skLineSegment(sketch, "E41.bottom", {"start": v(8.73, 7.98) * mm, "end": v(80.6, 7.98) * mm});
            skLineSegment(sketch, "E41.top", {"start": v(8.73, -7.88) * mm, "end": v(80.6, -7.88) * mm});
            skLineSegment(sketch, "E41.left", {"start": v(8.73, 7.98) * mm, "end": v(8.73, -7.88) * mm});
            skLineSegment(sketch, "E41.right", {"start": v(80.6, 7.98) * mm, "end": v(80.6, -7.88) * mm});
            skSolve(sketch);
        }
        {
            var Q0;
            Q0=makeQuery(id+"F34.imprint","IMPRINT",FACE,{"disambiguationData":[TD([[makeQuery(id+"F34.imprint","IMPRINT",EDGE,{"derivedFrom":sQuery(id+"F34.wireOp",EDGE,"E41.bottom")}),-1.0]])]});
            var Q1;
            {var subQ0=sQuery(id+"F2.wireOp",EDGE,"E10");var subQ1=makeQuery(id+"F15.boolean.opBoolean","MERGE",FACE,{"derivedFrom":[makeQuery(id+"F3.boolean.opBoolean","COPY",FACE,{"derivedFrom":makeQuery(id+"F3.opExtrude","SWEPT_FACE",FACE,{"disambiguationData":[OSD([subQ0])]})}),makeQuery(id+"F15.opExtrude","SWEPT_FACE",FACE,{"disambiguationData":[OSD([sQuery(id+"F0.wireOp",EDGE,"E1.top"),subQ0])]})]});Q1=makeQuery(id+"F21.imprint","IMPRINT",FACE,{"disambiguationData":[TD([[makeQuery(id+"F21.imprint","IMPRINT",EDGE,{"derivedFrom":makeQuery(id+"F16.boolean.opBoolean","INTERSECT",EDGE,{"derivedFrom":[subQ1,makeQuery(id+"F16.opExtrude","SWEPT_FACE",FACE,{"disambiguationData":[OSD([sQuery(id+"F0.wireOp",EDGE,"E6.bottom")])]})]})}),-1.0]])]});}
            extrude(context, id + "F35", {"entities" : qUnion([Q0, Q1]), "operationType" : NewBodyOperationType.ADD, "oppositeDirection" : true, "depth" : 1 * mm});
        }
        {
            var Q0;
            {var subQ0=sQuery(id+"F0.wireOp",EDGE,"E1.top");var subQ2=sQuery(id+"F2.wireOp",EDGE,"E9");Q0=makeQuery(id+"F33.boolean.opBoolean","MERGE",FACE,{"derivedFrom":[makeQuery(id+"F17.boolean.opBoolean","SPLIT",FACE,{"disambiguationData":[TD([makeQuery(id+"F1.opExtrude","SWEPT_FACE",FACE,{"disambiguationData":[OSD([sQuery(id+"F0.wireOp",EDGE,"E1.bottom")])]})])],"derivedFrom":makeQuery(id+"F15.boolean.opBoolean","MERGE",FACE,{"derivedFrom":[makeQuery(id+"F3.boolean.opBoolean","COPY",FACE,{"derivedFrom":makeQuery(id+"F3.opExtrude","SWEPT_FACE",FACE,{"disambiguationData":[OSD([subQ2])]})}),makeQuery(id+"F15.opExtrude","SWEPT_FACE",FACE,{"disambiguationData":[OSD([subQ0,subQ2])]})]})}),makeQuery(id+"F33.opExtrude","CAP_FACE",FACE,{"disambiguationData":[OSD([sQuery(id+"F32.wireOp",EDGE,"E40.bottom"),sQuery(id+"F32.wireOp",EDGE,"E40.top"),sQuery(id+"F32.wireOp",EDGE,"E40.left"),sQuery(id+"F32.wireOp",EDGE,"E40.right")])],"isStart":true})]});}
            var sketch = newSketch(context, id + "F36", { "sketchPlane" : qUnion([Q0])});
            skText(sketch, "E42", { "text": "www.simtrack.com.au", "fontName": "OpenSans-Regular.ttf"});
            skLineSegment(sketch, "E43", {"start": v(-59.66, 1.4) * mm, "end": v(-59.66, 9) * mm});
            skLineSegment(sketch, "E44", {"start": v(-63.79, -1.4) * mm, "end": v(-63.79, -9) * mm});
            const initialGuessF36  = {"E42": [-0.08379, -0.0014, 1, 0, 0.0028]};
            skSetInitialGuess(sketch, initialGuessF36);
            skSolve(sketch);
        }
        {
            var Q0;
            Q0=qSketchRegion(id+"F36",true);
            extrude(context, id + "F37", {"entities" : qUnion([Q0]), "operationType" : NewBodyOperationType.REMOVE, "oppositeDirection" : true, "depth" : .25 * mm});
        }
        {
            var Q0;
            {var subQ0=sQuery(id+"F2.wireOp",EDGE,"E10");var subQ1=sQuery(id+"F0.wireOp",EDGE,"E6.right");var subQ2=sQuery(id+"F0.wireOp",EDGE,"E6.left");var subQ3=sQuery(id+"F0.wireOp",EDGE,"E6.top");var subQ4=sQuery(id+"F0.wireOp",EDGE,"E6.bottom");var subQ5=sQuery(id+"F0.wireOp",EDGE,"E1.top");Q0=makeQuery(id+"F35.boolean.opBoolean","MERGE",FACE,{"derivedFrom":[makeQuery(id+"F17.boolean.opBoolean","SPLIT",FACE,{"disambiguationData":[TD([makeQuery(id+"F1.opExtrude","SWEPT_FACE",FACE,{"disambiguationData":[OSD([sQuery(id+"F0.wireOp",EDGE,"E1.bottom")])]})])],"derivedFrom":makeQuery(id+"F15.boolean.opBoolean","MERGE",FACE,{"derivedFrom":[makeQuery(id+"F3.boolean.opBoolean","COPY",FACE,{"derivedFrom":makeQuery(id+"F3.opExtrude","SWEPT_FACE",FACE,{"disambiguationData":[OSD([subQ0])]})}),makeQuery(id+"F15.opExtrude","SWEPT_FACE",FACE,{"disambiguationData":[OSD([subQ5,subQ0])]})]})}),makeQuery(id+"F35.opExtrude","CAP_FACE",FACE,{"disambiguationData":[OSD([subQ5,subQ4,subQ3,subQ2,subQ1,subQ0])],"isStart":true}),makeQuery(id+"F35.opExtrude","CAP_FACE",FACE,{"disambiguationData":[OSD([subQ5,subQ4,subQ3,subQ2,subQ1,subQ0,sQuery(id+"F34.wireOp",EDGE,"E41.bottom"),sQuery(id+"F34.wireOp",EDGE,"E41.top"),sQuery(id+"F34.wireOp",EDGE,"E41.left"),sQuery(id+"F34.wireOp",EDGE,"E41.right")])],"isStart":true})]});}
            var sketch = newSketch(context, id + "F38", { "sketchPlane" : qUnion([Q0])});
            skText(sketch, "E45", { "text": "made in Australia", "fontName": "OpenSans-Regular.ttf"});
            skLineSegment(sketch, "E46", {"start": v(58.79, 1.33) * mm, "end": v(58.79, 9) * mm});
            skLineSegment(sketch, "E47", {"start": v(58.79, -1.33) * mm, "end": v(58.79, -9) * mm});
            const initialGuessF38  = {"E45": [0.04379, -0.00133, 1, 0, 0.00266]};
            skSetInitialGuess(sketch, initialGuessF38);
            skSolve(sketch);
        }
        {
            var Q0;
            Q0=qSketchRegion(id+"F38",true);
            extrude(context, id + "F39", {"entities" : qUnion([Q0]), "operationType" : NewBodyOperationType.REMOVE, "oppositeDirection" : true, "depth" : .25 * mm});
        }
    });
